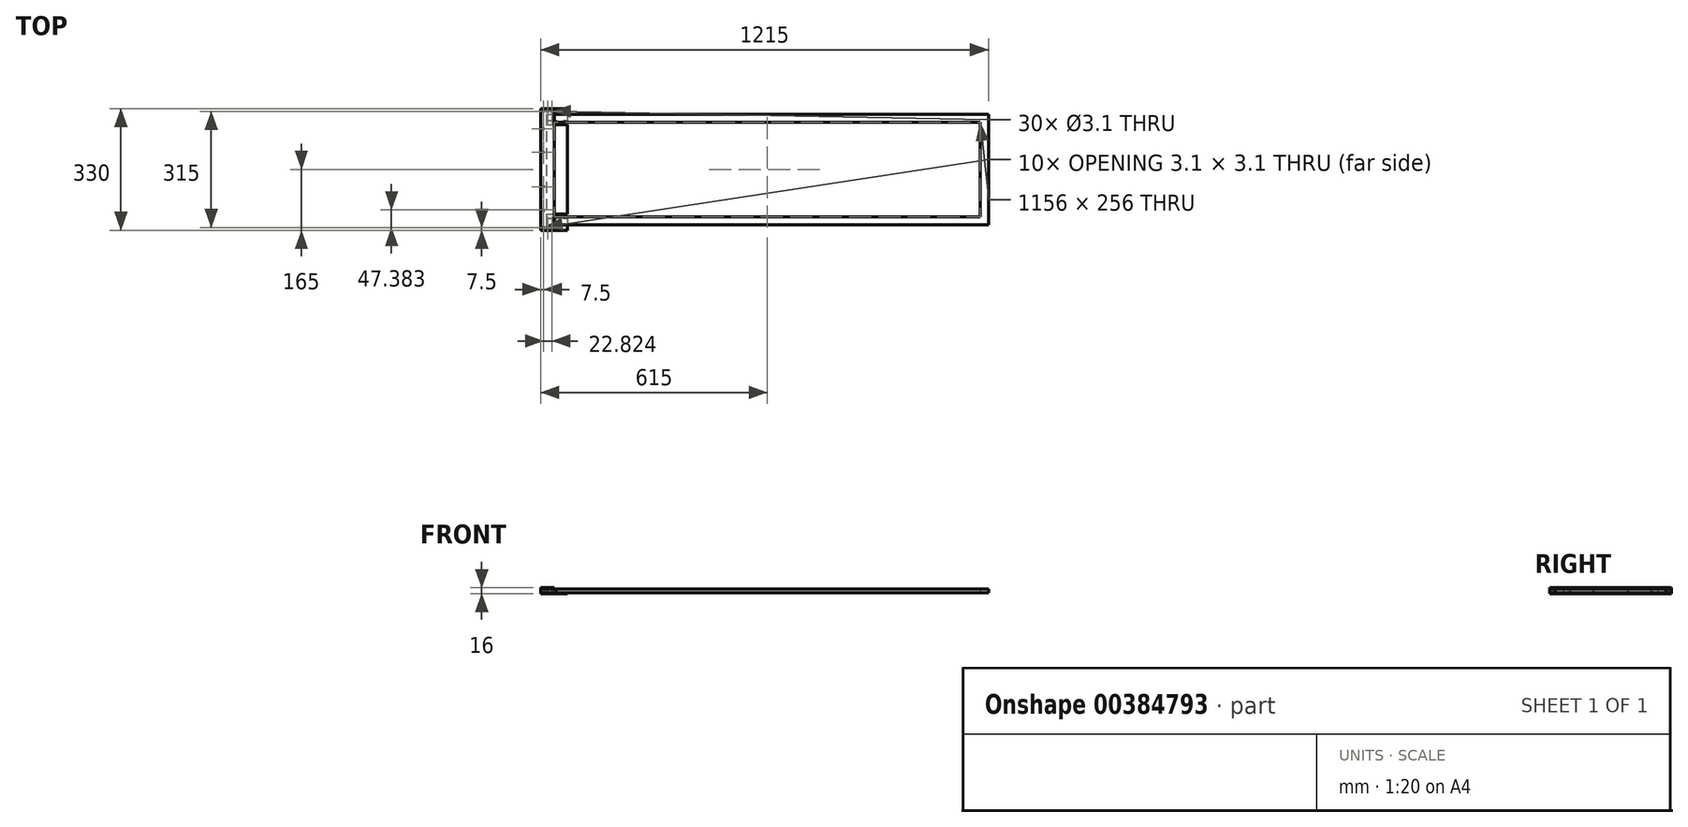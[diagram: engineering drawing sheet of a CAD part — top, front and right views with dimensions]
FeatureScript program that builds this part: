
annotation { "Feature Type Name" : "Feature", "Feature Type Description" : "" }
export const myFeature = defineFeature(function(context is Context, id is Id, definition is map)
    precondition{}
    {
        {
            var Q0;
            Q0=qCreatedBy(makeId("Top.planeOp"),FACE);
            var sketch = newSketch(context, id + "F0", { "sketchPlane" : qUnion([Q0])});
            skLineSegment(sketch, "E0.bottom", {"start": v(0, 0) * mm, "end": v(1200, 0) * mm});
            skLineSegment(sketch, "E0.top", {"start": v(0, -300) * mm, "end": v(1200, -300) * mm});
            skLineSegment(sketch, "E0.left", {"start": v(0, 0) * mm, "end": v(0, -300) * mm});
            skLineSegment(sketch, "E0.right", {"start": v(1200, 0) * mm, "end": v(1200, -300) * mm});
            skLineSegment(sketch, "E1.bottom", {"start": v(22, -22) * mm, "end": v(1178, -22) * mm});
            skLineSegment(sketch, "E1.top", {"start": v(22, -278) * mm, "end": v(1178, -278) * mm});
            skLineSegment(sketch, "E1.left", {"start": v(22, -22) * mm, "end": v(22, -278) * mm});
            skLineSegment(sketch, "E1.right", {"start": v(1178, -22) * mm, "end": v(1178, -278) * mm});
            skLineSegment(sketch, "E2.bottom", {"start": v(0, -29) * mm, "end": v(17, -29) * mm, "construction": true});
            skLineSegment(sketch, "E2.top", {"start": v(0, -17) * mm, "end": v(17, -17) * mm, "construction": true});
            skLineSegment(sketch, "E2.left", {"start": v(0, -29) * mm, "end": v(0, -17) * mm});
            skLineSegment(sketch, "E2.right", {"start": v(17, -29) * mm, "end": v(17, -17) * mm, "construction": true});
            skLineSegment(sketch, "E3", {"start": v(0, -150) * mm, "end": v(1200, -150) * mm, "construction": true});
            skLineSegment(sketch, "E4", {"start": v(600, 0) * mm, "end": v(600, -300) * mm, "construction": true});
            skLineSegment(sketch, "E5.MirrorCS", {"start": v(0, -283) * mm, "end": v(17, -283) * mm, "construction": true});
            skLineSegment(sketch, "E6.MirrorCS", {"start": v(17, -271) * mm, "end": v(17, -283) * mm, "construction": true});
            skLineSegment(sketch, "E7.MirrorCS", {"start": v(0, -271) * mm, "end": v(17, -271) * mm, "construction": true});
            skLineSegment(sketch, "E8.MirrorCS", {"start": v(1200, -17) * mm, "end": v(1183, -17) * mm, "construction": true});
            skLineSegment(sketch, "E9.MirrorCS", {"start": v(1183, -29) * mm, "end": v(1183, -17) * mm, "construction": true});
            skLineSegment(sketch, "E10.MirrorCS", {"start": v(1200, -29) * mm, "end": v(1183, -29) * mm, "construction": true});
            skLineSegment(sketch, "E11.MirrorCS", {"start": v(1200, -283) * mm, "end": v(1183, -283) * mm, "construction": true});
            skLineSegment(sketch, "E12.MirrorCS", {"start": v(1183, -271) * mm, "end": v(1183, -283) * mm, "construction": true});
            skLineSegment(sketch, "E13.MirrorCS", {"start": v(1200, -271) * mm, "end": v(1183, -271) * mm, "construction": true});
            skSolve(sketch);
        }
        {
            var Q0;
            Q0 = qSketchRegion(id + "F0", true);
            extrude(context, id + "F1", {"entities" : qUnion([Q0]), "depth" : 10 * mm});
        }
        {
            var Q0;
            {var subQ3=sQuery(id+"F0.wireOp",EDGE,"E0.bottom");Q0=makeQuery(id+"F0.imprint","IMPRINT",FACE,{"disambiguationData":[TD([[makeQuery(id+"F0.imprint","IMPRINT",EDGE,{"derivedFrom":subQ3}),-1.0]])]});}
            var sketch = newSketch(context, id + "F2", { "sketchPlane" : qUnion([Q0])});
            skPoint(sketch, "E14.0", {"position": v(0, 0) * mm});
            skPoint(sketch, "E14.1", {"position": v(0, -300) * mm});
            skLineSegment(sketch, "E15", {"start": v(0, 0) * mm, "end": v(0, -300) * mm});
            skLineSegment(sketch, "E16", {"start": v(27, -300) * mm, "end": v(27, -315) * mm});
            skLineSegment(sketch, "E17", {"start": v(27, -315) * mm, "end": v(-15, -315) * mm});
            skLineSegment(sketch, "E18", {"start": v(-15, -315) * mm, "end": v(-15, 15) * mm});
            skLineSegment(sketch, "E19", {"start": v(-15, 15) * mm, "end": v(27, 15) * mm});
            skLineSegment(sketch, "E20", {"start": v(27, 15) * mm, "end": v(27, 0) * mm});
            skLineSegment(sketch, "E21", {"start": v(27, 0) * mm, "end": v(0, 0) * mm});
            skLineSegment(sketch, "E22", {"start": v(0, -300) * mm, "end": v(27, -300) * mm});
            skLineSegment(sketch, "E23", {"start": v(27, 7.5) * mm, "end": v(-15, 7.5) * mm, "construction": true});
            skLineSegment(sketch, "E24", {"start": v(0, 0) * mm, "end": v(-15, 0) * mm, "construction": true});
            skPoint(sketch, "E24.endSnap0", {"position": v(-15, -150) * mm});
            skLineSegment(sketch, "E25", {"start": v(-7.5, 15) * mm, "end": v(-7.5, -315) * mm, "construction": true});
            skPoint(sketch, "E25.startSnap0", {"position": v(-7.5, 0) * mm});
            skLineSegment(sketch, "E26", {"start": v(27, -307.5) * mm, "end": v(-15, -307.5) * mm, "construction": true});
            skPoint(sketch, "E27", {"position": v(15.32, 7.5) * mm});
            skPoint(sketch, "E28", {"position": v(-7.5, -39.88) * mm});
            skPoint(sketch, "E29", {"position": v(-7.5, -103.02) * mm});
            skPoint(sketch, "E30.MirrorP", {"position": v(15.32, -307.5) * mm});
            skPoint(sketch, "E31.MirrorP", {"position": v(-7.5, -300) * mm});
            skPoint(sketch, "E32.MirrorP", {"position": v(-7.5, -260.12) * mm});
            skPoint(sketch, "E33.MirrorP", {"position": v(-7.5, -196.98) * mm});
            skPoint(sketch, "E34", {"position": v(-7.5, 7.5) * mm});
            skPoint(sketch, "E35", {"position": v(-7.5, -307.5) * mm});
            skLineSegment(sketch, "E36", {"start": v(-7.5, 7.5) * mm, "end": v(15.32, 7.5) * mm});
            skPoint(sketch, "E37", {"position": v(3.91, 7.5) * mm});
            skPoint(sketch, "E38.MirrorP", {"position": v(3.91, -307.5) * mm});
            skSolve(sketch);
        }
        {
            var Q0;
            Q0 = qSketchRegion(id + "F2", true);
            extrude(context, id + "F3", {"entities" : qUnion([Q0]), "depth" : 10 * mm});
        }
        {
            var Q0;
            Q0=makeQuery(id+"F3.opExtrude","CAP_FACE",FACE,{"disambiguationData":[OSD([sQuery(id+"F2.wireOp",EDGE,"E15"),sQuery(id+"F2.wireOp",EDGE,"E16"),sQuery(id+"F2.wireOp",EDGE,"E17"),sQuery(id+"F2.wireOp",EDGE,"E18"),sQuery(id+"F2.wireOp",EDGE,"E19"),sQuery(id+"F2.wireOp",EDGE,"E20"),sQuery(id+"F2.wireOp",EDGE,"E21"),sQuery(id+"F2.wireOp",EDGE,"E22")])],"isStart":true});
            var sketch = newSketch(context, id + "F4", { "sketchPlane" : qUnion([Q0])});
            skLineSegment(sketch, "E39.0", {"start": v(22, 22) * mm, "end": v(22, 278) * mm});
            skLineSegment(sketch, "E39.1", {"start": v(-15, -15) * mm, "end": v(27, -15) * mm});
            skLineSegment(sketch, "E39.2", {"start": v(27, 315) * mm, "end": v(-15, 315) * mm});
            skLineSegment(sketch, "E40", {"start": v(-15, 315) * mm, "end": v(-15, -15) * mm});
            skLineSegment(sketch, "E41", {"start": v(57, -15) * mm, "end": v(57, 17) * mm});
            skLineSegment(sketch, "E42", {"start": v(27, 315) * mm, "end": v(57, 315) * mm});
            skLineSegment(sketch, "E43", {"start": v(27, -15) * mm, "end": v(57, -15) * mm});
            skPoint(sketch, "E44.0", {"position": v(0, 283) * mm});
            skPoint(sketch, "E44.1", {"position": v(0, 271) * mm});
            skPoint(sketch, "E44.2", {"position": v(0, 17) * mm});
            skPoint(sketch, "E44.3", {"position": v(0, 29) * mm});
            skLineSegment(sketch, "E45.bottom", {"start": v(0, 283) * mm, "end": v(57, 283) * mm});
            skLineSegment(sketch, "E45.top", {"start": v(0, 271) * mm, "end": v(57, 271) * mm});
            skLineSegment(sketch, "E45.left", {"start": v(0, 283) * mm, "end": v(0, 271) * mm});
            skLineSegment(sketch, "E46.bottom", {"start": v(0, 29) * mm, "end": v(57, 29) * mm});
            skLineSegment(sketch, "E46.top", {"start": v(0, 17) * mm, "end": v(57, 17) * mm});
            skLineSegment(sketch, "E46.left", {"start": v(0, 29) * mm, "end": v(0, 17) * mm});
            skLineSegment(sketch, "E47.trimOffspring", {"start": v(57, 29) * mm, "end": v(57, 271) * mm});
            skLineSegment(sketch, "E48.trimOffspring", {"start": v(57, 283) * mm, "end": v(57, 315) * mm});
            skPoint(sketch, "E49", {"position": v(37, 251) * mm});
            skPoint(sketch, "E50.MirrorP", {"position": v(37, 49) * mm});
            skSolve(sketch);
        }
        {
            var Q0;
            Q0 = qSketchRegion(id + "F4", true);
            extrude(context, id + "F5", {"entities" : qUnion([Q0]), "depth" : 3 * mm});
        }
        {
            var Q0;
            Q0=makeQuery(id+"F3.opExtrude","CAP_FACE",FACE,{"disambiguationData":[OSD([sQuery(id+"F2.wireOp",EDGE,"E15"),sQuery(id+"F2.wireOp",EDGE,"E16"),sQuery(id+"F2.wireOp",EDGE,"E17"),sQuery(id+"F2.wireOp",EDGE,"E18"),sQuery(id+"F2.wireOp",EDGE,"E19"),sQuery(id+"F2.wireOp",EDGE,"E20"),sQuery(id+"F2.wireOp",EDGE,"E21"),sQuery(id+"F2.wireOp",EDGE,"E22")])],"isStart":false});
            var sketch = newSketch(context, id + "F6", { "sketchPlane" : qUnion([Q0])});
            skLineSegment(sketch, "E51.0", {"start": v(22, -29) * mm, "end": v(22, -271) * mm});
            skLineSegment(sketch, "E51.1", {"start": v(-15, -315) * mm, "end": v(-15, 15) * mm});
            skLineSegment(sketch, "E52", {"start": v(-15, 15) * mm, "end": v(22, 15) * mm});
            skLineSegment(sketch, "E53", {"start": v(22, 15) * mm, "end": v(22, -17) * mm});
            skLineSegment(sketch, "E54", {"start": v(22, -283) * mm, "end": v(22, -315) * mm});
            skLineSegment(sketch, "E55", {"start": v(22, -315) * mm, "end": v(-15, -315) * mm});
            skPoint(sketch, "E56.0", {"position": v(17, -17) * mm});
            skPoint(sketch, "E56.1", {"position": v(0, -17) * mm});
            skPoint(sketch, "E56.2", {"position": v(17, -29) * mm});
            skPoint(sketch, "E56.3", {"position": v(17, -271) * mm});
            skPoint(sketch, "E56.4", {"position": v(0, -271) * mm});
            skPoint(sketch, "E56.5", {"position": v(17, -283) * mm});
            skPoint(sketch, "E57.orphan", {"position": v(22, -22) * mm});
            skPoint(sketch, "E58.orphan", {"position": v(22, -278) * mm});
            skPoint(sketch, "E59.top.end.orphan", {"position": v(0, -283) * mm});
            skLineSegment(sketch, "E60", {"start": v(22, -271) * mm, "end": v(22, -283) * mm});
            skLineSegment(sketch, "E61", {"start": v(22, -29) * mm, "end": v(22, -17) * mm});
            skSolve(sketch);
        }
        {
            var Q0;
            Q0 = qSketchRegion(id + "F6", true);
            extrude(context, id + "F7", {"entities" : qUnion([Q0]), "depth" : 3 * mm});
        }
        {
            var Q0;
            Q0=sQuery(id+"F2.wireOp",VERTEX,"E27");
            var Q1;
            Q1=sQuery(id+"F2.wireOp",VERTEX,"E28");
            var Q2;
            Q2=sQuery(id+"F2.wireOp",VERTEX,"E33.MirrorP");
            var Q3;
            Q3=sQuery(id+"F2.wireOp",VERTEX,"E32.MirrorP");
            var Q4;
            Q4=sQuery(id+"F2.wireOp",VERTEX,"E30.MirrorP");
            var Q5;
            Q5=sQuery(id+"F2.wireOp",VERTEX,"E29");
            var Q6;
            Q6=sQuery(id+"F2.wireOp",VERTEX,"E35");
            var Q7;
            Q7=sQuery(id+"F2.wireOp",VERTEX,"E34");
            var Q8;
            Q8=sQuery(id+"F2.wireOp",VERTEX,"a67ea658-6ea6-4be2-8c02-e4a60680756b");
            var Q9;
            Q9=sQuery(id+"F2.wireOp",VERTEX,"72cfb018-354c-4e97-814c-121f1cbe6bf4");
            var Q10;
            Q10=sQuery(id+"F2.wireOp",VERTEX,"E38.MirrorP");
            var Q11;
            Q11=sQuery(id+"F2.wireOp",VERTEX,"E37");
            var Q12;
            Q12=makeQuery(id+"F3.opExtrude","SWEPT_BODY",BODY,{"disambiguationData":[OSD([sQuery(id+"F2.wireOp",EDGE,"E15"),sQuery(id+"F2.wireOp",EDGE,"E16"),sQuery(id+"F2.wireOp",EDGE,"E17"),sQuery(id+"F2.wireOp",EDGE,"E18"),sQuery(id+"F2.wireOp",EDGE,"E19"),sQuery(id+"F2.wireOp",EDGE,"E20"),sQuery(id+"F2.wireOp",EDGE,"E21"),sQuery(id+"F2.wireOp",EDGE,"E22")])]});
            var Q13;
            Q13=makeQuery(id+"F5.opExtrude","SWEPT_BODY",BODY,{"disambiguationData":[OSD([sQuery(id+"F4.wireOp",EDGE,"E39.1"),sQuery(id+"F4.wireOp",EDGE,"E39.2"),sQuery(id+"F4.wireOp",EDGE,"E40"),sQuery(id+"F4.wireOp",EDGE,"E41"),sQuery(id+"F4.wireOp",EDGE,"E42"),sQuery(id+"F4.wireOp",EDGE,"E43")])]});
            var Q14;
            Q14=makeQuery(id+"F7.opExtrude","SWEPT_BODY",BODY,{"disambiguationData":[OSD([sQuery(id+"F6.wireOp",EDGE,"E51.0"),sQuery(id+"F6.wireOp",EDGE,"E51.1"),sQuery(id+"F6.wireOp",EDGE,"E52"),sQuery(id+"F6.wireOp",EDGE,"E53"),sQuery(id+"F6.wireOp",EDGE,"E54"),sQuery(id+"F6.wireOp",EDGE,"E55")])]});
            hole(context, id + "F8", {"style" : HoleStyle.SIMPLE, "endStyle" : HoleEndStyle.THROUGH, "oppositeDirection" : true, "holeDiameter" : 3.1 * mm, "isTappedThrough" : true, "tappedDepth" : 12 * mm, "tapClearance" : 3, "locations" : qUnion([Q0, Q1, Q2, Q3, Q4, Q5, Q6, Q7, Q8, Q9, Q10, Q11]), "scope" : qUnion([Q12, Q13, Q14])});
        }
        {
            var Q0;
            Q0=sQuery(id+"F2.wireOp",VERTEX,"E30.MirrorP");
            var Q1;
            Q1=sQuery(id+"F2.wireOp",VERTEX,"944f6098-9e1c-488d-8f8a-1d9249b8956a0.MirrorP");
            var Q2;
            Q2=sQuery(id+"F2.wireOp",VERTEX,"E32.MirrorP");
            var Q3;
            Q3=sQuery(id+"F2.wireOp",VERTEX,"E33.MirrorP");
            var Q4;
            Q4=sQuery(id+"F2.wireOp",VERTEX,"E29");
            var Q5;
            Q5=sQuery(id+"F2.wireOp",VERTEX,"E28");
            var Q6;
            Q6=sQuery(id+"F2.wireOp",VERTEX,"0626636d-2abf-488d-8283-141f30d5ce65");
            var Q7;
            Q7=sQuery(id+"F2.wireOp",VERTEX,"E27");
            var Q8;
            Q8=sQuery(id+"F4.wireOp",VERTEX,"E49");
            var Q9;
            Q9=sQuery(id+"F4.wireOp",VERTEX,"E50.MirrorP");
            var Q10;
            Q10=sQuery(id+"F2.wireOp",VERTEX,"E37");
            var Q11;
            Q11=sQuery(id+"F2.wireOp",VERTEX,"E34");
            var Q12;
            Q12=sQuery(id+"F2.wireOp",VERTEX,"E35");
            var Q13;
            Q13=sQuery(id+"F2.wireOp",VERTEX,"E38.MirrorP");
            var Q14;
            Q14=makeQuery(id+"F5.opExtrude","SWEPT_BODY",BODY,{"disambiguationData":[OSD([sQuery(id+"F4.wireOp",EDGE,"E39.1"),sQuery(id+"F4.wireOp",EDGE,"E39.2"),sQuery(id+"F4.wireOp",EDGE,"E40"),sQuery(id+"F4.wireOp",EDGE,"E41"),sQuery(id+"F4.wireOp",EDGE,"E42"),sQuery(id+"F4.wireOp",EDGE,"E43")])]});
            hole(context, id + "F9", {"style" : HoleStyle.SIMPLE, "endStyle" : HoleEndStyle.THROUGH, "holeDiameter" : 3.1 * mm, "isTappedThrough" : true, "tappedDepth" : 12 * mm, "tapClearance" : 3, "locations" : qUnion([Q0, Q1, Q2, Q3, Q4, Q5, Q6, Q7, Q8, Q9, Q10, Q11, Q12, Q13]), "scope" : qUnion([Q14])});
        }
    });
